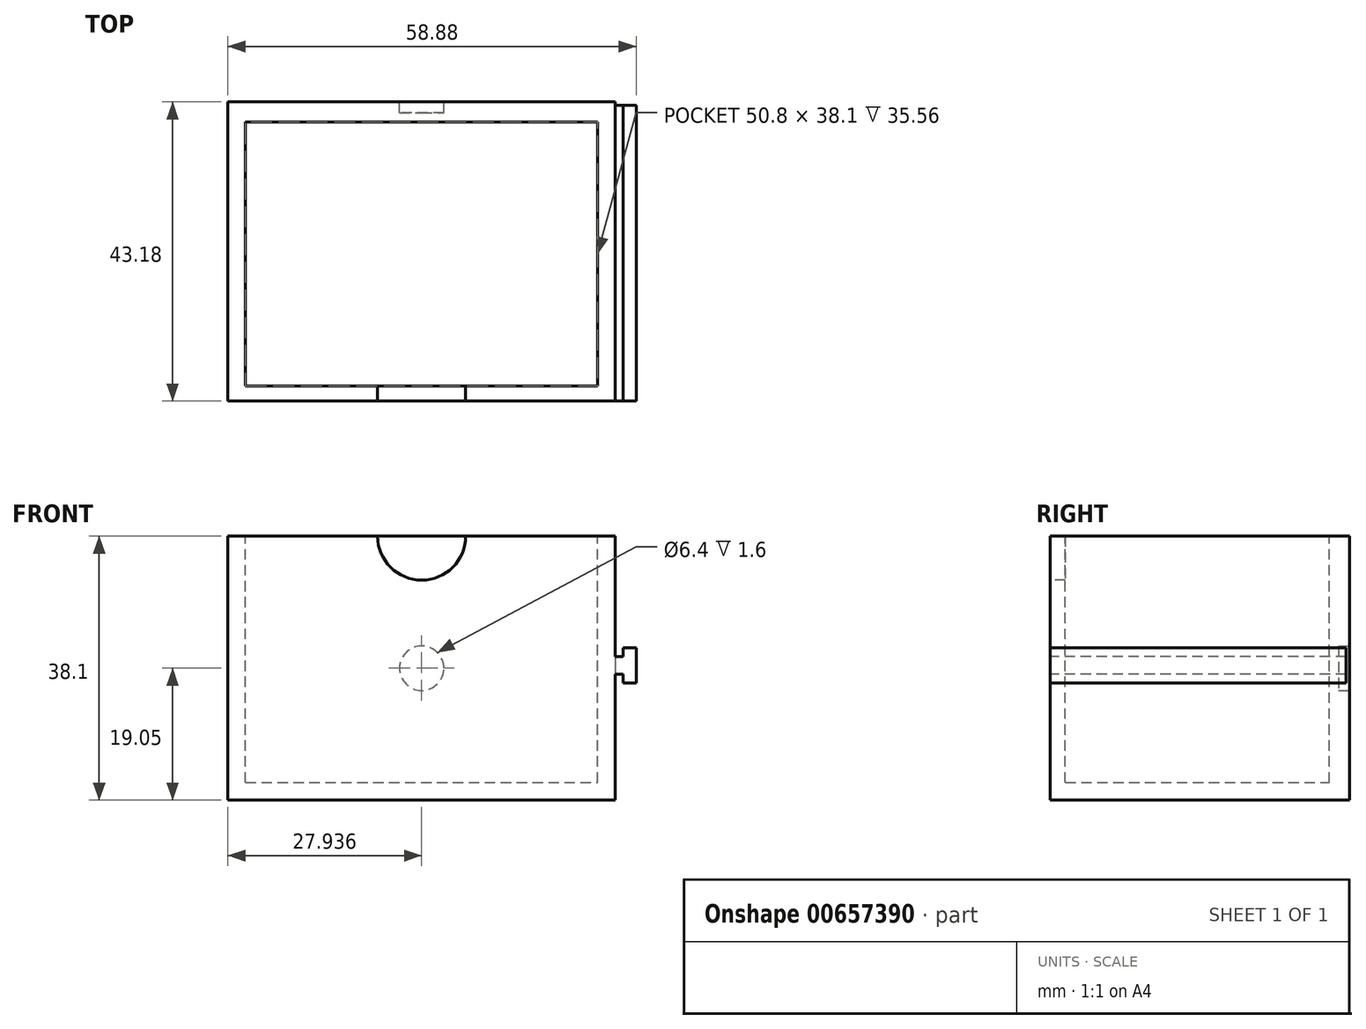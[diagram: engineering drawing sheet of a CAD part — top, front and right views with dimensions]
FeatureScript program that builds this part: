
annotation { "Feature Type Name" : "Feature", "Feature Type Description" : "" }
export const myFeature = defineFeature(function(context is Context, id is Id, definition is map)
    precondition{}
    {
        {
            var Q0;
            Q0=qCreatedBy(makeId("Front.planeOp"),FACE);
            var sketch = newSketch(context, id + "F0", { "sketchPlane" : qUnion([Q0])});
            skLineSegment(sketch, "E0.bottom", {"start": v(-48.42, 38.1) * mm, "end": v(7.46, 38.1) * mm});
            skLineSegment(sketch, "E0.top", {"start": v(-48.42, 0) * mm, "end": v(7.46, 0) * mm});
            skLineSegment(sketch, "E0.left", {"start": v(-48.42, 38.1) * mm, "end": v(-48.42, 0) * mm});
            skLineSegment(sketch, "E0.right", {"start": v(7.46, 38.1) * mm, "end": v(7.46, 0) * mm});
            skSolve(sketch);
        }
        {
            var Q0;
            Q0 = qSketchRegion(id + "F0", true);
            extrude(context, id + "F1", {"entities" : qUnion([Q0]), "oppositeDirection" : true, "depth" : 43.18 * mm, "offsetDistance" : 25.4 * mm});
        }
        {
            var Q0;
            Q0=makeQuery(id+"F1.opExtrude","SWEPT_FACE",FACE,{"disambiguationData":[OSD([sQuery(id+"F0.wireOp",EDGE,"E0.bottom")])]});
            var sketch = newSketch(context, id + "F2", { "sketchPlane" : qUnion([Q0])});
            skLineSegment(sketch, "E1.bottom", {"start": v(-45.88, 2.17) * mm, "end": v(4.92, 2.17) * mm});
            skLineSegment(sketch, "E1.top", {"start": v(-45.88, 40.27) * mm, "end": v(4.92, 40.27) * mm});
            skLineSegment(sketch, "E1.left", {"start": v(-45.88, 2.17) * mm, "end": v(-45.88, 40.27) * mm});
            skLineSegment(sketch, "E1.right", {"start": v(4.92, 2.17) * mm, "end": v(4.92, 40.27) * mm});
            skSolve(sketch);
        }
        {
            var Q0;
            Q0 = qSketchRegion(id + "F2", true);
            extrude(context, id + "F3", {"entities" : qUnion([Q0]), "operationType" : NewBodyOperationType.REMOVE, "oppositeDirection" : true, "depth" : 35.56 * mm, "offsetDistance" : 25.4 * mm});
        }
        {
            var Q0;
            Q0=makeQuery(id+"F1.opExtrude","CAP_FACE",FACE,{"disambiguationData":[OSD([sQuery(id+"F0.wireOp",EDGE,"E0.bottom"),sQuery(id+"F0.wireOp",EDGE,"E0.top"),sQuery(id+"F0.wireOp",EDGE,"E0.left"),sQuery(id+"F0.wireOp",EDGE,"E0.right")])],"isStart":true});
            var sketch = newSketch(context, id + "F4", { "sketchPlane" : qUnion([Q0])});
            skCircle(sketch, "E2", {"center": v(-20.48, 38.1) * mm, "radius": 6.35 * mm});
            skSolve(sketch);
        }
        {
            var Q0;
            Q0 = qSketchRegion(id + "F4", true);
            extrude(context, id + "F5", {"entities" : qUnion([Q0]), "operationType" : NewBodyOperationType.REMOVE, "oppositeDirection" : true, "depth" : 25.4 * mm, "offsetDistance" : 25.4 * mm});
        }
        {
            var Q0;
            Q0=makeQuery(id+"F1.opExtrude","CAP_FACE",FACE,{"disambiguationData":[OSD([sQuery(id+"F0.wireOp",EDGE,"E0.bottom"),sQuery(id+"F0.wireOp",EDGE,"E0.top"),sQuery(id+"F0.wireOp",EDGE,"E0.left"),sQuery(id+"F0.wireOp",EDGE,"E0.right")])],"isStart":false});
            var sketch = newSketch(context, id + "F6", { "sketchPlane" : qUnion([Q0])});
            skCircle(sketch, "E3", {"center": v(20.48, 19.05) * mm, "radius": 3.2 * mm});
            skPoint(sketch, "E3.centerSnap0", {"position": v(-7.46, 19.05) * mm});
            skPoint(sketch, "E3.centerSnap1", {"position": v(20.48, 38.1) * mm});
            skSolve(sketch);
        }
        {
            var Q0;
            Q0 = qSketchRegion(id + "F6", true);
            extrude(context, id + "F7", {"entities" : qUnion([Q0]), "operationType" : NewBodyOperationType.REMOVE, "oppositeDirection" : true, "depth" : 1.6 * mm, "offsetDistance" : 25.4 * mm});
        }
        {
            var Q0;
            Q0=makeQuery(id+"F1.opExtrude","CAP_FACE",FACE,{"disambiguationData":[OSD([sQuery(id+"F0.wireOp",EDGE,"E0.bottom"),sQuery(id+"F0.wireOp",EDGE,"E0.top"),sQuery(id+"F0.wireOp",EDGE,"E0.left"),sQuery(id+"F0.wireOp",EDGE,"E0.right")])],"isStart":true});
            var sketch = newSketch(context, id + "F8", { "sketchPlane" : qUnion([Q0])});
            skLineSegment(sketch, "E4.bottom", {"start": v(8.56, 20.74) * mm, "end": v(6.65, 20.74) * mm});
            skLineSegment(sketch, "E4.top", {"start": v(8.56, 18.2) * mm, "end": v(6.65, 18.2) * mm});
            skPoint(sketch, "E4.middle", {"position": v(7.29, 19.47) * mm});
            skLineSegment(sketch, "E5.bottom", {"start": v(10.46, 22.01) * mm, "end": v(8.56, 22.01) * mm});
            skLineSegment(sketch, "E5.top", {"start": v(10.46, 16.93) * mm, "end": v(8.56, 16.93) * mm});
            skLineSegment(sketch, "E5.left", {"start": v(10.46, 22.01) * mm, "end": v(10.46, 16.93) * mm});
            skLineSegment(sketch, "E6", {"start": v(8.56, 20.74) * mm, "end": v(8.56, 22.01) * mm});
            skLineSegment(sketch, "E7", {"start": v(8.56, 18.2) * mm, "end": v(8.56, 16.93) * mm});
            skSolve(sketch);
        }
        {
            var Q0;
            Q0=makeQuery(id+"F8.imprint","IMPRINT",FACE,{"disambiguationData":[TD([[makeQuery(id+"F8.imprint","IMPRINT",EDGE,{"derivedFrom":sQuery(id+"F8.wireOp",EDGE,"E5.bottom")}),1.0]])]});
            extrude(context, id + "F9", {"entities" : qUnion([Q0]), "operationType" : NewBodyOperationType.ADD, "oppositeDirection" : true, "depth" : 42.67 * mm, "offsetDistance" : 25.4 * mm});
        }
    });
